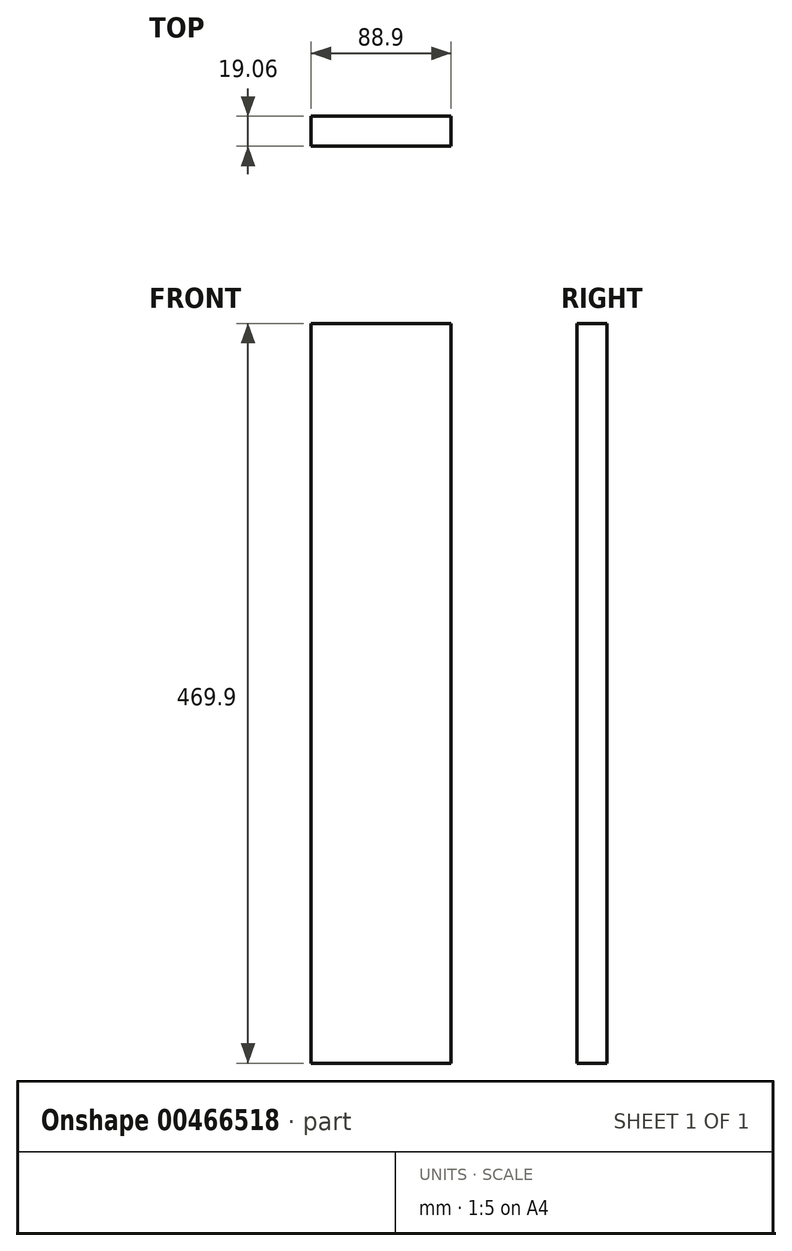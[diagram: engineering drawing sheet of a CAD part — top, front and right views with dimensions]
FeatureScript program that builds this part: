
annotation { "Feature Type Name" : "Feature", "Feature Type Description" : "" }
export const myFeature = defineFeature(function(context is Context, id is Id, definition is map)
    precondition{}
    {
        {
            var Q0;
            Q0=qCreatedBy(makeId("Top.planeOp"),FACE);
            var sketch = newSketch(context, id + "F0", { "sketchPlane" : qUnion([Q0])});
            skLineSegment(sketch, "E0.bottom", {"start": v(44.45, -9.53) * mm, "end": v(-44.45, -9.53) * mm});
            skLineSegment(sketch, "E0.top", {"start": v(44.45, 9.53) * mm, "end": v(-44.45, 9.53) * mm});
            skLineSegment(sketch, "E0.left", {"start": v(44.45, -9.53) * mm, "end": v(44.45, 9.52) * mm});
            skLineSegment(sketch, "E0.right", {"start": v(-44.45, -9.53) * mm, "end": v(-44.45, 9.52) * mm});
            skPoint(sketch, "E0.middle", {"position": v(0, 0) * mm});
            skSolve(sketch);
        }
        {
            var Q0;
            Q0=makeQuery(id+"F0.imprint","IMPRINT",FACE,{"disambiguationData":[TD([[makeQuery(id+"F0.imprint","IMPRINT",EDGE,{"derivedFrom":sQuery(id+"F0.wireOp",EDGE,"E0.bottom")}),-1.0]])]});
            extrude(context, id + "F1", {"entities" : qUnion([Q0]), "depth" : 469.9 * mm});
        }
    });
